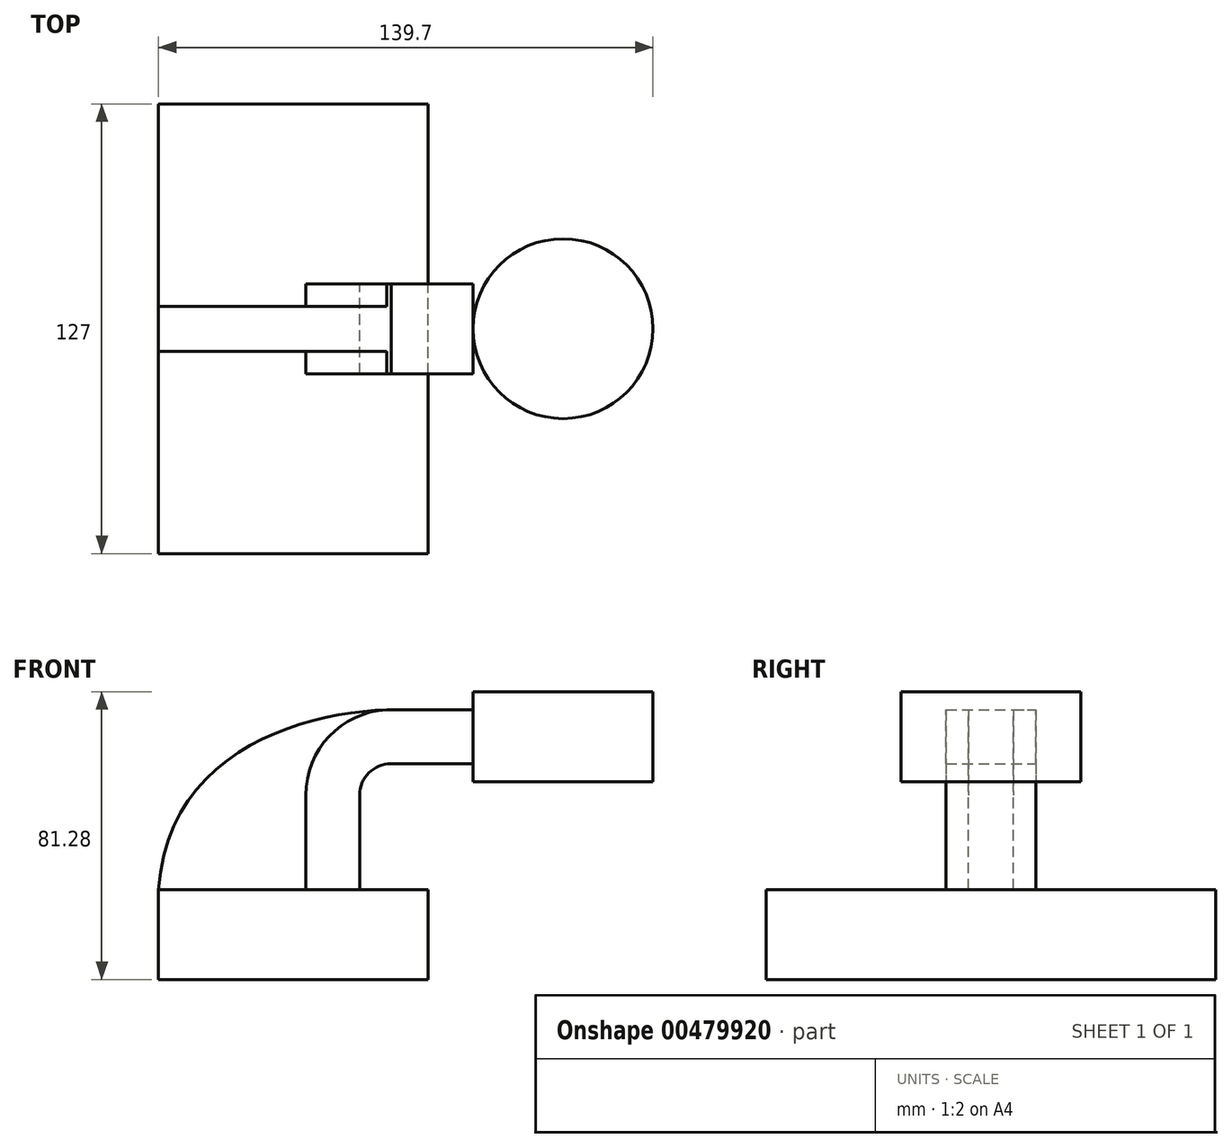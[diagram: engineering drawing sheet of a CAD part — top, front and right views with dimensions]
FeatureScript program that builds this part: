
annotation { "Feature Type Name" : "Feature", "Feature Type Description" : "" }
export const myFeature = defineFeature(function(context is Context, id is Id, definition is map)
    precondition{}
    {
        {
            var Q0;
            Q0=qCreatedBy(makeId("Front.planeOp"),FACE);
            var sketch = newSketch(context, id + "F0", { "sketchPlane" : qUnion([Q0])});
            skLineSegment(sketch, "E0.bottom", {"start": v(38.1, -12.7) * mm, "end": v(-38.1, -12.7) * mm});
            skLineSegment(sketch, "E0.top", {"start": v(38.1, 12.7) * mm, "end": v(-38.1, 12.7) * mm});
            skLineSegment(sketch, "E0.left", {"start": v(38.1, -12.7) * mm, "end": v(38.1, 12.7) * mm});
            skLineSegment(sketch, "E0.right", {"start": v(-38.1, -12.7) * mm, "end": v(-38.1, 12.7) * mm});
            skPoint(sketch, "E0.middle", {"position": v(0, 0) * mm});
            skLineSegment(sketch, "E1.bottom", {"start": v(101.6, 43.18) * mm, "end": v(50.8, 43.18) * mm});
            skLineSegment(sketch, "E1.top", {"start": v(101.6, 68.58) * mm, "end": v(50.8, 68.58) * mm});
            skLineSegment(sketch, "E1.left", {"start": v(101.6, 43.18) * mm, "end": v(101.6, 68.58) * mm});
            skLineSegment(sketch, "E1.right", {"start": v(50.8, 43.18) * mm, "end": v(50.8, 68.58) * mm});
            skPoint(sketch, "E1.middle", {"position": v(76.2, 55.88) * mm});
            skLineSegment(sketch, "E2", {"start": v(18.76, 12.7) * mm, "end": v(18.76, 39.37) * mm});
            skArc(sketch, "E3", {"start": v(18.76, 39.37) * mm, "mid": v(21.36, 45.66) * mm, "end": v(27.65, 48.26) * mm});
            skLineSegment(sketch, "E4", {"start": v(27.65, 48.26) * mm, "end": v(61.83, 48.26) * mm});
            skLineSegment(sketch, "E5.0", {"start": v(27.65, 63.5) * mm, "end": v(62.08, 63.5) * mm});
            skArc(sketch, "E5.1", {"start": v(3.52, 39.37) * mm, "mid": v(10.58, 56.43) * mm, "end": v(27.65, 63.5) * mm});
            skLineSegment(sketch, "E5.2", {"start": v(3.52, 12.7) * mm, "end": v(3.52, 39.37) * mm});
            skLineSegment(sketch, "E6", {"start": v(76.2, 68.58) * mm, "end": v(76.2, 43.18) * mm});
            skFitSpline(sketch, "E7", {"points": [v(-38.1, 12.7) * mm, v(27.65, 63.5) * mm], "startDerivative": vector(8.4, 119.06) * mm, "endDerivative": vector(72.39, 1.44) * mm});
            skSolve(sketch);
        }
        {
            var Q0;
            Q0=makeQuery(id+"F0.imprint","IMPRINT",FACE,{"disambiguationData":[TD([[makeQuery(id+"F0.imprint","IMPRINT",EDGE,{"derivedFrom":sQuery(id+"F0.wireOp",EDGE,"E0.bottom")}),-1.0]])]});
            extrude(context, id + "F1", {"entities" : qUnion([Q0]), "endBound" : BoundingType.SYMMETRIC, "depth" : 127 * mm});
        }
        {
            var Q0;
            {var subQ1=sQuery(id+"F0.wireOp",EDGE,"E2");Q0=makeQuery(id+"F0.imprint","IMPRINT",FACE,{"disambiguationData":[TD([[makeQuery(id+"F0.imprint","IMPRINT",EDGE,{"derivedFrom":subQ1}),1.0]])]});}
            extrude(context, id + "F2", {"entities" : qUnion([Q0]), "operationType" : NewBodyOperationType.ADD, "endBound" : BoundingType.SYMMETRIC, "depth" : 25.4 * mm});
        }
        {
            var Q0;
            {var subQ3=sQuery(id+"F0.wireOp",EDGE,"E5.2");Q0=makeQuery(id+"F0.imprint","IMPRINT",FACE,{"disambiguationData":[TD([[makeQuery(id+"F0.imprint","IMPRINT",EDGE,{"derivedFrom":subQ3}),1.0]])]});}
            extrude(context, id + "F3", {"entities" : qUnion([Q0]), "operationType" : NewBodyOperationType.ADD, "endBound" : BoundingType.SYMMETRIC, "depth" : 12.7 * mm});
        }
        {
            var Q0;
            {var subQ0=sQuery(id+"F0.wireOp",EDGE,"E1.left");Q0=makeQuery(id+"F0.imprint","IMPRINT",FACE,{"disambiguationData":[TD([[makeQuery(id+"F0.imprint","IMPRINT",EDGE,{"derivedFrom":subQ0}),1.0]])]});}
            var Q1;
            Q1=sQuery(id+"F0.wireOp",EDGE,"E6");
            revolve(context, id + "F4", {"operationType" : NewBodyOperationType.ADD, "entities" : qUnion([Q0]), "axis" : qUnion([Q1]), "revolveType" : RevolveType.FULL});
        }
    });
